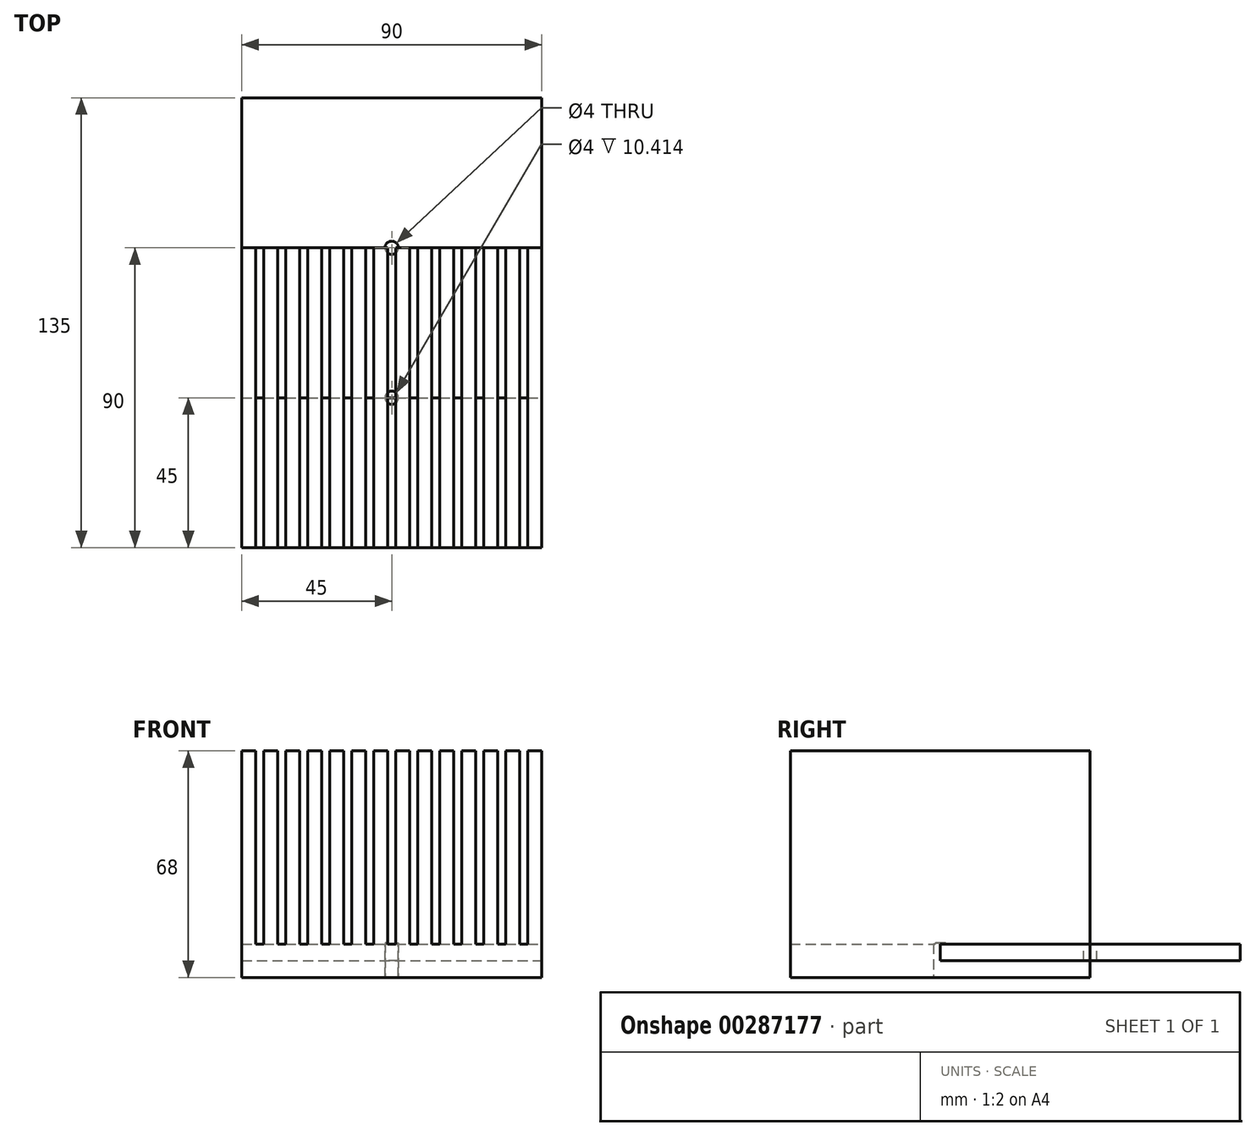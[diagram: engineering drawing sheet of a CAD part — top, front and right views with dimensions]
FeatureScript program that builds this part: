
annotation { "Feature Type Name" : "Feature", "Feature Type Description" : "" }
export const myFeature = defineFeature(function(context is Context, id is Id, definition is map)
    precondition{}
    {
        {
            var Q0;
            Q0=qCreatedBy(makeId("Front.planeOp"),FACE);
            var sketch = newSketch(context, id + "F0", { "sketchPlane" : qUnion([Q0])});
            skLineSegment(sketch, "E0", {"start": v(0, 0) * mm, "end": v(31.86, 0) * mm, "construction": true});
            skLineSegment(sketch, "E1", {"start": v(0, 0) * mm, "end": v(0, 23.9) * mm, "construction": true});
            skLineSegment(sketch, "E2.bottom", {"start": v(-45, -5) * mm, "end": v(45, -5) * mm});
            skLineSegment(sketch, "E2.top", {"start": v(-40.85, 5) * mm, "end": v(-38.4, 5) * mm});
            skLineSegment(sketch, "E2.left", {"start": v(-45, -5) * mm, "end": v(-45, 5) * mm});
            skLineSegment(sketch, "E2.right", {"start": v(45, -5) * mm, "end": v(45, 5) * mm});
            skPoint(sketch, "E2.middle", {"position": v(0, 0) * mm});
            skLineSegment(sketch, "E3", {"start": v(-45, 5) * mm, "end": v(-45, 63) * mm});
            skLineSegment(sketch, "E4", {"start": v(-45, 63) * mm, "end": v(-40.85, 63) * mm});
            skLineSegment(sketch, "E5", {"start": v(-40.85, 63) * mm, "end": v(-40.85, 5) * mm});
            skLineSegment(sketch, "E6.1.0.0", {"start": v(-38.4, 63) * mm, "end": v(-34.25, 63) * mm});
            skLineSegment(sketch, "E6.1.0.1", {"start": v(-34.25, 63) * mm, "end": v(-34.25, 5) * mm});
            skLineSegment(sketch, "E6.1.0.2", {"start": v(-38.4, 5) * mm, "end": v(-38.4, 63) * mm});
            skLineSegment(sketch, "E6.2.0.0", {"start": v(-31.8, 63) * mm, "end": v(-27.64, 63) * mm});
            skLineSegment(sketch, "E6.2.0.1", {"start": v(-27.64, 63) * mm, "end": v(-27.64, 5) * mm});
            skLineSegment(sketch, "E6.2.0.2", {"start": v(-31.8, 5) * mm, "end": v(-31.8, 63) * mm});
            skLineSegment(sketch, "E6.3.0.0", {"start": v(-25.19, 63) * mm, "end": v(-21.04, 63) * mm});
            skLineSegment(sketch, "E6.3.0.1", {"start": v(-21.04, 63) * mm, "end": v(-21.04, 5) * mm});
            skLineSegment(sketch, "E6.3.0.2", {"start": v(-25.19, 5) * mm, "end": v(-25.19, 63) * mm});
            skLineSegment(sketch, "E6.4.0.0", {"start": v(-18.58, 63) * mm, "end": v(-14.44, 63) * mm});
            skLineSegment(sketch, "E6.4.0.1", {"start": v(-14.44, 63) * mm, "end": v(-14.44, 5) * mm});
            skLineSegment(sketch, "E6.4.0.2", {"start": v(-18.58, 5) * mm, "end": v(-18.58, 63) * mm});
            skLineSegment(sketch, "E6.5.0.0", {"start": v(-11.98, 63) * mm, "end": v(-7.83, 63) * mm});
            skLineSegment(sketch, "E6.5.0.1", {"start": v(-7.83, 63) * mm, "end": v(-7.83, 5) * mm});
            skLineSegment(sketch, "E6.5.0.2", {"start": v(-11.98, 5) * mm, "end": v(-11.98, 63) * mm});
            skLineSegment(sketch, "E6.6.0.0", {"start": v(-5.38, 63) * mm, "end": v(-1.23, 63) * mm});
            skLineSegment(sketch, "E6.6.0.1", {"start": v(-1.23, 63) * mm, "end": v(-1.23, 5) * mm});
            skLineSegment(sketch, "E6.6.0.2", {"start": v(-5.38, 5) * mm, "end": v(-5.38, 63) * mm});
            skLineSegment(sketch, "E6.7.0.0", {"start": v(1.23, 63) * mm, "end": v(5.38, 63) * mm});
            skLineSegment(sketch, "E6.7.0.1", {"start": v(5.38, 63) * mm, "end": v(5.38, 5) * mm});
            skLineSegment(sketch, "E6.7.0.2", {"start": v(1.23, 5) * mm, "end": v(1.23, 63) * mm});
            skLineSegment(sketch, "E6.8.0.0", {"start": v(7.83, 63) * mm, "end": v(11.98, 63) * mm});
            skLineSegment(sketch, "E6.8.0.1", {"start": v(11.98, 63) * mm, "end": v(11.98, 5) * mm});
            skLineSegment(sketch, "E6.8.0.2", {"start": v(7.83, 5) * mm, "end": v(7.83, 63) * mm});
            skLineSegment(sketch, "E6.9.0.0", {"start": v(14.44, 63) * mm, "end": v(18.58, 63) * mm});
            skLineSegment(sketch, "E6.9.0.1", {"start": v(18.58, 63) * mm, "end": v(18.58, 5) * mm});
            skLineSegment(sketch, "E6.9.0.2", {"start": v(14.44, 5) * mm, "end": v(14.44, 63) * mm});
            skLineSegment(sketch, "E6.10.0.0", {"start": v(21.04, 63) * mm, "end": v(25.19, 63) * mm});
            skLineSegment(sketch, "E6.10.0.1", {"start": v(25.19, 63) * mm, "end": v(25.19, 5) * mm});
            skLineSegment(sketch, "E6.10.0.2", {"start": v(21.04, 5) * mm, "end": v(21.04, 63) * mm});
            skLineSegment(sketch, "E6.11.0.0", {"start": v(27.64, 63) * mm, "end": v(31.8, 63) * mm});
            skLineSegment(sketch, "E6.11.0.1", {"start": v(31.8, 63) * mm, "end": v(31.8, 5) * mm});
            skLineSegment(sketch, "E6.11.0.2", {"start": v(27.64, 5) * mm, "end": v(27.64, 63) * mm});
            skLineSegment(sketch, "E6.12.0.0", {"start": v(34.25, 63) * mm, "end": v(38.4, 63) * mm});
            skLineSegment(sketch, "E6.12.0.1", {"start": v(38.4, 63) * mm, "end": v(38.4, 5) * mm});
            skLineSegment(sketch, "E6.12.0.2", {"start": v(34.25, 5) * mm, "end": v(34.25, 63) * mm});
            skLineSegment(sketch, "E6.13.0.0", {"start": v(40.85, 63) * mm, "end": v(45, 63) * mm});
            skLineSegment(sketch, "E6.13.0.1", {"start": v(45, 63) * mm, "end": v(45, 5) * mm});
            skLineSegment(sketch, "E6.13.0.2", {"start": v(40.85, 5) * mm, "end": v(40.85, 63) * mm});
            skLineSegment(sketch, "E6.direction1", {"start": v(-40.85, 5) * mm, "end": v(-38.4, 5) * mm, "construction": true});
            skLineSegment(sketch, "E7.trimOffspring", {"start": v(-34.25, 5) * mm, "end": v(-31.8, 5) * mm});
            skLineSegment(sketch, "E8.trimOffspring", {"start": v(-27.64, 5) * mm, "end": v(-25.19, 5) * mm});
            skLineSegment(sketch, "E9.trimOffspring", {"start": v(-21.04, 5) * mm, "end": v(-18.58, 5) * mm});
            skLineSegment(sketch, "E10.trimOffspring", {"start": v(-14.44, 5) * mm, "end": v(-11.98, 5) * mm});
            skLineSegment(sketch, "E11.trimOffspring", {"start": v(-7.83, 5) * mm, "end": v(-5.38, 5) * mm});
            skLineSegment(sketch, "E12.trimOffspring", {"start": v(-1.23, 5) * mm, "end": v(1.23, 5) * mm});
            skLineSegment(sketch, "E13.trimOffspring", {"start": v(5.38, 5) * mm, "end": v(7.83, 5) * mm});
            skLineSegment(sketch, "E14.trimOffspring", {"start": v(11.98, 5) * mm, "end": v(14.44, 5) * mm});
            skLineSegment(sketch, "E15.trimOffspring", {"start": v(18.58, 5) * mm, "end": v(21.04, 5) * mm});
            skLineSegment(sketch, "E16.trimOffspring", {"start": v(25.19, 5) * mm, "end": v(27.64, 5) * mm});
            skLineSegment(sketch, "E17.trimOffspring", {"start": v(31.8, 5) * mm, "end": v(34.25, 5) * mm});
            skLineSegment(sketch, "E18.trimOffspring", {"start": v(38.4, 5) * mm, "end": v(40.85, 5) * mm});
            skSolve(sketch);
        }
        {
            var Q0;
            Q0 = qSketchRegion(id + "F0", true);
            extrude(context, id + "F1", {"entities" : qUnion([Q0]), "depth" : 90 * mm});
        }
        {
            var Q0;
            Q0=makeQuery(id+"F1.opExtrude","SWEPT_FACE",FACE,{"disambiguationData":[OSD([sQuery(id+"F0.wireOp",EDGE,"E2.bottom")])]});
            var sketch = newSketch(context, id + "F2", { "sketchPlane" : qUnion([Q0])});
            skLineSegment(sketch, "E19", {"start": v(-15, 90) * mm, "end": v(-15, 0) * mm, "construction": true});
            skLineSegment(sketch, "E20", {"start": v(15, 90) * mm, "end": v(15, 0) * mm, "construction": true});
            skLineSegment(sketch, "E21", {"start": v(-45, 60) * mm, "end": v(45, 60) * mm, "construction": true});
            skLineSegment(sketch, "E22", {"start": v(-45, 30) * mm, "end": v(45, 30) * mm, "construction": true});
            skPoint(sketch, "E23", {"position": v(-15, 60) * mm});
            skPoint(sketch, "E24", {"position": v(15, 60) * mm});
            skPoint(sketch, "E25", {"position": v(-15, 30) * mm});
            skPoint(sketch, "E26", {"position": v(15, 30) * mm});
            skLineSegment(sketch, "E27", {"start": v(-45, 90) * mm, "end": v(45, 0) * mm, "construction": true});
            skLineSegment(sketch, "E28", {"start": v(-45, 0) * mm, "end": v(45, 90) * mm, "construction": true});
            skPoint(sketch, "E29", {"position": v(0, 45) * mm});
            skCircle(sketch, "E30", {"center": v(0, 45) * mm, "radius": 2 * mm});
            skSolve(sketch);
        }
        {
            var Q0;
            Q0 = qSketchRegion(id + "F2", true);
            extrude(context, id + "F3", {"entities" : qUnion([Q0]), "operationType" : NewBodyOperationType.REMOVE, "oppositeDirection" : true, "depth" : 10.4 * mm});
        }
        {
            var Q0;
            Q0=qCreatedBy(makeId("Top.planeOp"),FACE);
            var sketch = newSketch(context, id + "F4", { "sketchPlane" : qUnion([Q0])});
            skLineSegment(sketch, "E31.bottom", {"start": v(-45, 45) * mm, "end": v(45, 45) * mm});
            skLineSegment(sketch, "E31.top", {"start": v(-45, -45) * mm, "end": v(45, -45) * mm});
            skLineSegment(sketch, "E31.left", {"start": v(-45, 45) * mm, "end": v(-45, -45) * mm});
            skLineSegment(sketch, "E31.right", {"start": v(45, 45) * mm, "end": v(45, -45) * mm});
            skPoint(sketch, "E31.middle", {"position": v(0, 0) * mm});
            skSolve(sketch);
        }
        {
            var Q0;
            Q0 = qSketchRegion(id + "F4", true);
            extrude(context, id + "F5", {"entities" : qUnion([Q0]), "depth" : 5 * mm});
        }
        {
            var Q0;
            Q0=makeQuery(id+"F5.opExtrude","CAP_FACE",FACE,{"disambiguationData":[OSD([sQuery(id+"F4.wireOp",EDGE,"E31.bottom"),sQuery(id+"F4.wireOp",EDGE,"E31.top"),sQuery(id+"F4.wireOp",EDGE,"E31.left"),sQuery(id+"F4.wireOp",EDGE,"E31.right")])],"isStart":false});
            var sketch = newSketch(context, id + "F6", { "sketchPlane" : qUnion([Q0])});
            skCircle(sketch, "E32", {"center": v(0, 0) * mm, "radius": 2 * mm});
            skSolve(sketch);
        }
        {
            var Q0;
            Q0 = qSketchRegion(id + "F6", true);
            extrude(context, id + "F7", {"entities" : qUnion([Q0]), "operationType" : NewBodyOperationType.REMOVE, "oppositeDirection" : true, "depth" : 25.4 * mm});
        }
    });
